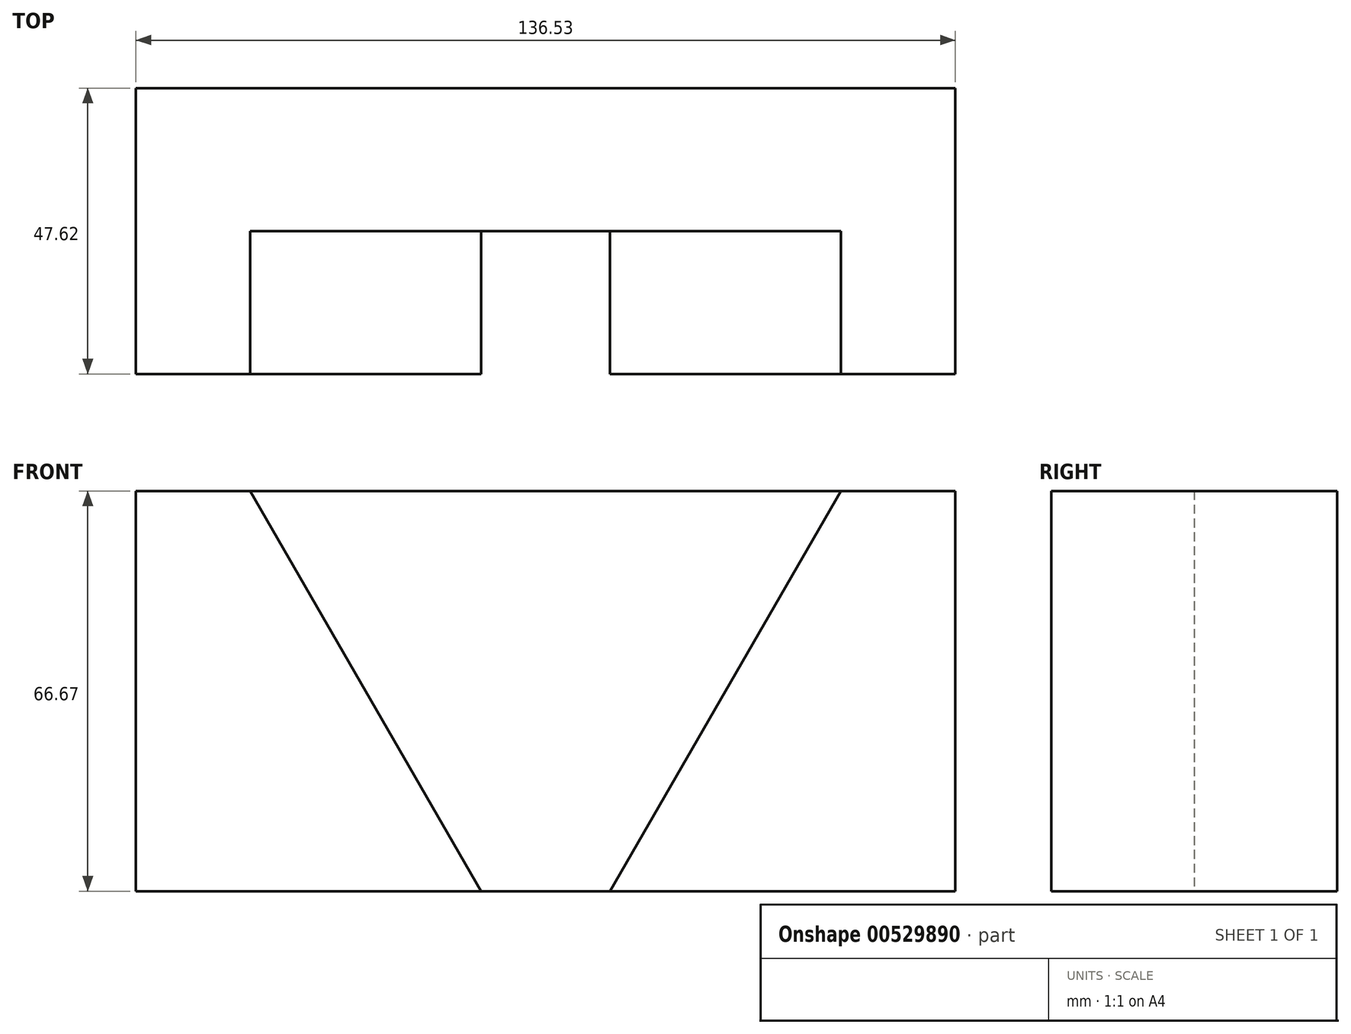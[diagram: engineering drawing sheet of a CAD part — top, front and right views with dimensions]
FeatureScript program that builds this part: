
annotation { "Feature Type Name" : "Feature", "Feature Type Description" : "" }
export const myFeature = defineFeature(function(context is Context, id is Id, definition is map)
    precondition{}
    {
        {
            var Q0;
            Q0=qCreatedBy(makeId("Front.planeOp"),FACE);
            var sketch = newSketch(context, id + "F0", { "sketchPlane" : qUnion([Q0])});
            skLineSegment(sketch, "E0.bottom", {"start": v(-66.12, 23.01) * mm, "end": v(70.4, 23.01) * mm});
            skLineSegment(sketch, "E0.top", {"start": v(-66.12, -43.66) * mm, "end": v(70.4, -43.66) * mm});
            skLineSegment(sketch, "E0.left", {"start": v(-66.12, 23.01) * mm, "end": v(-66.12, -43.66) * mm});
            skLineSegment(sketch, "E0.right", {"start": v(70.4, 23.01) * mm, "end": v(70.4, -43.66) * mm});
            skSolve(sketch);
        }
        {
            var Q0;
            Q0 = qSketchRegion(id + "F0", true);
            extrude(context, id + "F1", {"entities" : qUnion([Q0]), "depth" : 47.62 * mm, "offsetDistance" : 25.4 * mm});
        }
        {
            var Q0;
            Q0=makeQuery(id+"F1.opExtrude","CAP_FACE",FACE,{"disambiguationData":[OSD([sQuery(id+"F0.wireOp",EDGE,"E0.bottom"),sQuery(id+"F0.wireOp",EDGE,"E0.top"),sQuery(id+"F0.wireOp",EDGE,"E0.left"),sQuery(id+"F0.wireOp",EDGE,"E0.right")])],"isStart":false});
            var sketch = newSketch(context, id + "F2", { "sketchPlane" : qUnion([Q0])});
            skLineSegment(sketch, "E1", {"start": v(-47.07, 23.01) * mm, "end": v(-8.57, -43.66) * mm});
            skLineSegment(sketch, "E2", {"start": v(12.86, -43.66) * mm, "end": v(51.36, 23.01) * mm});
            skSolve(sketch);
        }
        {
            var Q0;
            {var subQ0=sQuery(id+"F2.wireOp",EDGE,"E1");Q0=makeQuery(id+"F2.imprint","IMPRINT",FACE,{"disambiguationData":[TD([[makeQuery(id+"F2.imprint","IMPRINT",EDGE,{"derivedFrom":subQ0}),1.0]])]});}
            extrude(context, id + "F3", {"entities" : qUnion([Q0]), "operationType" : NewBodyOperationType.REMOVE, "oppositeDirection" : true, "depth" : 23.8 * mm, "offsetDistance" : 25.4 * mm});
        }
    });
